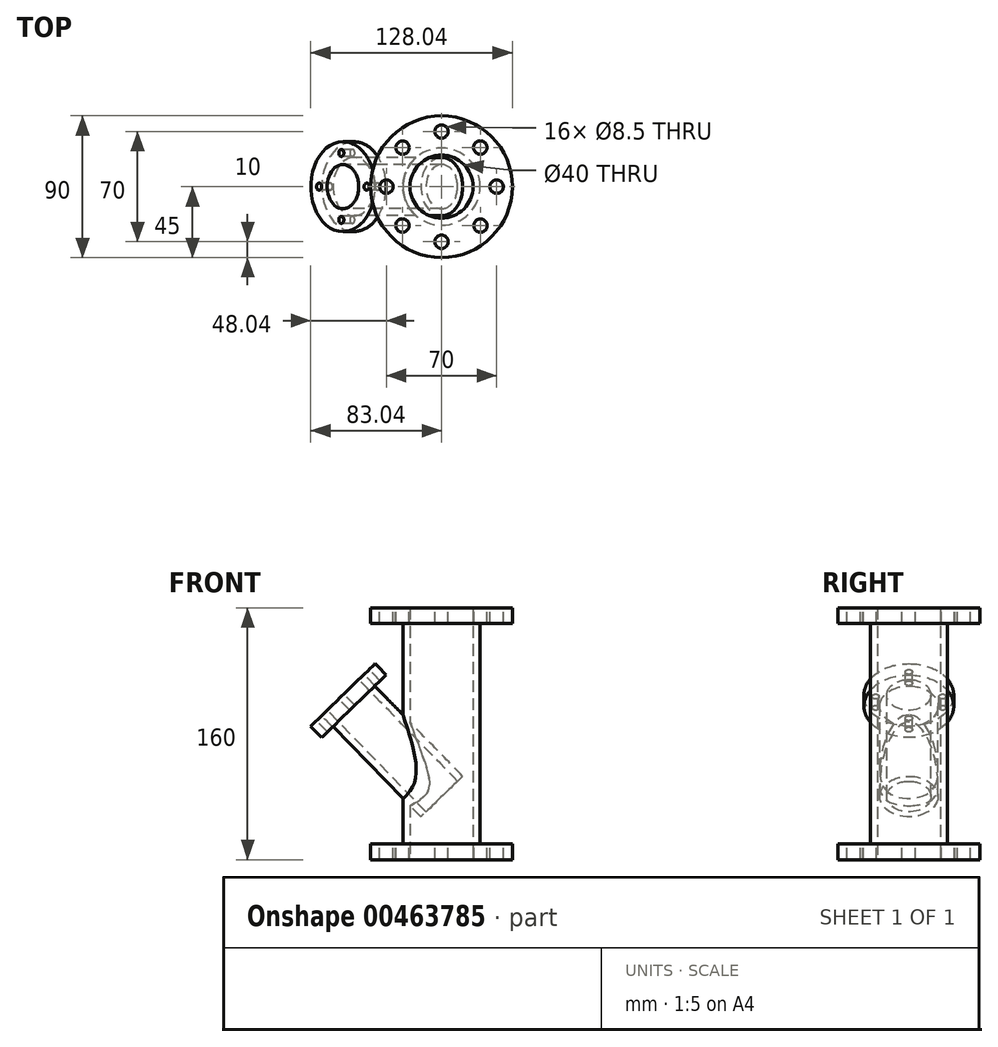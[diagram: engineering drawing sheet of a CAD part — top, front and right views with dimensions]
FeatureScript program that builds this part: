
annotation { "Feature Type Name" : "Feature", "Feature Type Description" : "" }
export const myFeature = defineFeature(function(context is Context, id is Id, definition is map)
    precondition{}
    {
        {
            var Q0;
            Q0=qCreatedBy(makeId("Top.planeOp"),FACE);
            var sketch = newSketch(context, id + "F0", { "sketchPlane" : qUnion([Q0])});
            skCircle(sketch, "E0", {"center": v(0, 0) * mm, "radius": 45 * mm});
            skSolve(sketch);
        }
        {
            var Q0;
            Q0=makeQuery(id+"F0.imprint","IMPRINT",FACE,{"disambiguationData":[TD([[makeQuery(id+"F0.imprint","IMPRINT",EDGE,{"derivedFrom":sQuery(id+"F0.wireOp",EDGE,"E0")}),1.0]])]});
            extrude(context, id + "F1", {"entities" : qUnion([Q0]), "depth" : 10 * mm});
        }
        {
            var Q0;
            Q0=makeQuery(id+"F1.opExtrude","CAP_FACE",FACE,{"disambiguationData":[OSD([sQuery(id+"F0.wireOp",EDGE,"E0")])],"isStart":false});
            var sketch = newSketch(context, id + "F2", { "sketchPlane" : qUnion([Q0])});
            skCircle(sketch, "E1", {"center": v(0, 0) * mm, "radius": 24.5 * mm});
            skCircle(sketch, "E2", {"center": v(0, 0) * mm, "radius": 20 * mm});
            skSolve(sketch);
        }
        {
            var Q0;
            Q0=makeQuery(id+"F2.imprint","IMPRINT",FACE,{"disambiguationData":[TD([[makeQuery(id+"F2.imprint","IMPRINT",EDGE,{"derivedFrom":sQuery(id+"F2.wireOp",EDGE,"E1")}),1.0]])]});
            extrude(context, id + "F3", {"entities" : qUnion([Q0]), "operationType" : NewBodyOperationType.ADD, "depth" : 140 * mm});
        }
        {
            var Q0;
            Q0=makeQuery(id+"F1.opExtrude","CAP_FACE",FACE,{"disambiguationData":[OSD([sQuery(id+"F0.wireOp",EDGE,"E0")])],"isStart":true});
            var sketch = newSketch(context, id + "F4", { "sketchPlane" : qUnion([Q0])});
            skCircle(sketch, "E3", {"center": v(0, 0) * mm, "radius": 20 * mm});
            skSolve(sketch);
        }
        {
            var Q0;
            Q0=makeQuery(id+"F4.imprint","IMPRINT",FACE,{"disambiguationData":[TD([[makeQuery(id+"F4.imprint","IMPRINT",EDGE,{"derivedFrom":sQuery(id+"F4.wireOp",EDGE,"E3")}),1.0]])]});
            extrude(context, id + "F5", {"entities" : qUnion([Q0]), "operationType" : NewBodyOperationType.REMOVE, "endBound" : BoundingType.THROUGH_ALL, "oppositeDirection" : true, "depth" : 25 * mm});
        }
        {
            var Q0;
            Q0=makeQuery(id+"F3.opExtrude","CAP_FACE",FACE,{"disambiguationData":[OSD([sQuery(id+"F2.wireOp",EDGE,"E1"),sQuery(id+"F2.wireOp",EDGE,"E2")])],"isStart":false});
            var sketch = newSketch(context, id + "F6", { "sketchPlane" : qUnion([Q0])});
            skCircle(sketch, "E4", {"center": v(0, 0) * mm, "radius": 45 * mm});
            skCircle(sketch, "E5", {"center": v(0, 0) * mm, "radius": 20 * mm});
            skSolve(sketch);
        }
        {
            var Q0;
            Q0 = qSketchRegion(id + "F6", true);
            extrude(context, id + "F7", {"entities" : qUnion([Q0]), "operationType" : NewBodyOperationType.ADD, "depth" : 10 * mm});
        }
        {
            var Q0;
            Q0=makeQuery(id+"F7.opExtrude","CAP_FACE",FACE,{"disambiguationData":[OSD([sQuery(id+"F6.wireOp",EDGE,"E4"),sQuery(id+"F6.wireOp",EDGE,"E5")])],"isStart":false});
            var sketch = newSketch(context, id + "F8", { "sketchPlane" : qUnion([Q0])});
            skCircle(sketch, "E6", {"center": v(0, 35) * mm, "radius": 4.25 * mm});
            skCircle(sketch, "E7", {"center": v(0, -35) * mm, "radius": 4.25 * mm});
            skCircle(sketch, "E8", {"center": v(35, 0) * mm, "radius": 4.25 * mm});
            skCircle(sketch, "E9", {"center": v(-35, 0) * mm, "radius": 4.25 * mm});
            skCircle(sketch, "E10", {"center": v(-24.73, 24.76) * mm, "radius": 4.25 * mm});
            skCircle(sketch, "E11", {"center": v(24.73, -24.76) * mm, "radius": 4.25 * mm});
            skCircle(sketch, "E12", {"center": v(24.64, 24.86) * mm, "radius": 4.25 * mm});
            skCircle(sketch, "E13", {"center": v(-24.83, -24.67) * mm, "radius": 4.25 * mm});
            skSolve(sketch);
        }
        {
            var Q0;
            Q0=makeQuery(id+"F8.imprint","IMPRINT",FACE,{"disambiguationData":[TD([[makeQuery(id+"F8.imprint","IMPRINT",EDGE,{"derivedFrom":sQuery(id+"F8.wireOp",EDGE,"E6")}),1.0]])]});
            var Q1;
            Q1=makeQuery(id+"F8.imprint","IMPRINT",FACE,{"disambiguationData":[TD([[makeQuery(id+"F8.imprint","IMPRINT",EDGE,{"derivedFrom":sQuery(id+"F8.wireOp",EDGE,"E7")}),1.0]])]});
            var Q2;
            Q2=makeQuery(id+"F8.imprint","IMPRINT",FACE,{"disambiguationData":[TD([[makeQuery(id+"F8.imprint","IMPRINT",EDGE,{"derivedFrom":sQuery(id+"F8.wireOp",EDGE,"E8")}),1.0]])]});
            var Q3;
            Q3=makeQuery(id+"F8.imprint","IMPRINT",FACE,{"disambiguationData":[TD([[makeQuery(id+"F8.imprint","IMPRINT",EDGE,{"derivedFrom":sQuery(id+"F8.wireOp",EDGE,"E9")}),1.0]])]});
            var Q4;
            Q4=makeQuery(id+"F8.imprint","IMPRINT",FACE,{"disambiguationData":[TD([[makeQuery(id+"F8.imprint","IMPRINT",EDGE,{"derivedFrom":sQuery(id+"F8.wireOp",EDGE,"E10")}),1.0]])]});
            var Q5;
            Q5=makeQuery(id+"F8.imprint","IMPRINT",FACE,{"disambiguationData":[TD([[makeQuery(id+"F8.imprint","IMPRINT",EDGE,{"derivedFrom":sQuery(id+"F8.wireOp",EDGE,"E11")}),1.0]])]});
            var Q6;
            Q6=makeQuery(id+"F8.imprint","IMPRINT",FACE,{"disambiguationData":[TD([[makeQuery(id+"F8.imprint","IMPRINT",EDGE,{"derivedFrom":sQuery(id+"F8.wireOp",EDGE,"E13")}),1.0]])]});
            var Q7;
            Q7=makeQuery(id+"F8.imprint","IMPRINT",FACE,{"disambiguationData":[TD([[makeQuery(id+"F8.imprint","IMPRINT",EDGE,{"derivedFrom":sQuery(id+"F8.wireOp",EDGE,"E12")}),1.0]])]});
            extrude(context, id + "F9", {"entities" : qUnion([Q0, Q1, Q2, Q3, Q4, Q5, Q6, Q7]), "operationType" : NewBodyOperationType.REMOVE, "endBound" : BoundingType.THROUGH_ALL, "oppositeDirection" : true, "depth" : 25 * mm});
        }
        {
            var Q0;
            Q0=qCreatedBy(makeId("Front.planeOp"),FACE);
            var sketch = newSketch(context, id + "F10", { "sketchPlane" : qUnion([Q0])});
            skLineSegment(sketch, "E14", {"start": v(-63.62, 103.65) * mm, "end": v(-43.2, 123.52) * mm});
            skLineSegment(sketch, "E15", {"start": v(-63.62, 103.65) * mm, "end": v(-84.05, 83.77) * mm});
            skSolve(sketch);
        }
        {
            var Q0;
            Q0=qCreatedBy(makeId("Right.planeOp"),FACE);
            var Q1;
            Q1=sQuery(id+"F10.wireOp",EDGE,"E15");
            cPlane(context, id + "F11", {"entities" : qUnion([Q0, Q1]), "cplaneType" : CPlaneType.LINE_ANGLE, "offset" : 25 * mm, "angle" : 0 * degree, "width" : 150 * mm, "height" : 150 * mm});
        }
        {
            var Q0;
            Q0=qCreatedBy(id+"F11.planeOp",FACE);
            var sketch = newSketch(context, id + "F12", { "sketchPlane" : qUnion([Q0])});
            skCircle(sketch, "E16", {"center": v(28.09, 0) * mm, "radius": 18.5 * mm});
            skSolve(sketch);
        }
        {
            var Q0;
            Q0 = qSketchRegion(id + "F12", true);
            extrude(context, id + "F13", {"entities" : qUnion([Q0]), "operationType" : NewBodyOperationType.ADD, "oppositeDirection" : true, "depth" : 90 * mm});
        }
        {
            var Q0;
            Q0=makeQuery(id+"F13.opExtrude","CAP_FACE",FACE,{"disambiguationData":[OSD([sQuery(id+"F12.wireOp",EDGE,"E16")])],"isStart":true});
            var sketch = newSketch(context, id + "F14", { "sketchPlane" : qUnion([Q0])});
            skCircle(sketch, "E17", {"center": v(28.09, 0) * mm, "radius": 28.5 * mm});
            skSolve(sketch);
        }
        {
            var Q0;
            Q0 = qSketchRegion(id + "F14", true);
            extrude(context, id + "F15", {"entities" : qUnion([Q0]), "operationType" : NewBodyOperationType.ADD, "oppositeDirection" : true, "depth" : 10 * mm});
        }
        {
            var Q0;
            Q0=makeQuery(id+"F15.boolean.opBoolean","MERGE",FACE,{"derivedFrom":[makeQuery(id+"F13.opExtrude","CAP_FACE",FACE,{"disambiguationData":[OSD([sQuery(id+"F12.wireOp",EDGE,"E16")])],"isStart":true}),makeQuery(id+"F15.opExtrude","CAP_FACE",FACE,{"disambiguationData":[OSD([sQuery(id+"F14.wireOp",EDGE,"E17")])],"isStart":true})]});
            var sketch = newSketch(context, id + "F16", { "sketchPlane" : qUnion([Q0])});
            skCircle(sketch, "E18", {"center": v(28.09, 0) * mm, "radius": 14 * mm});
            skSolve(sketch);
        }
        {
            var Q0;
            Q0=makeQuery(id+"F16.imprint","IMPRINT",FACE,{"disambiguationData":[TD([[makeQuery(id+"F16.imprint","IMPRINT",EDGE,{"derivedFrom":sQuery(id+"F16.wireOp",EDGE,"E18")}),1.0]])]});
            extrude(context, id + "F17", {"entities" : qUnion([Q0]), "operationType" : NewBodyOperationType.REMOVE, "oppositeDirection" : true, "depth" : 90 * mm});
        }
        {
            var Q0;
            Q0=makeQuery(id+"F15.boolean.opBoolean","MERGE",FACE,{"derivedFrom":[makeQuery(id+"F13.opExtrude","CAP_FACE",FACE,{"disambiguationData":[OSD([sQuery(id+"F12.wireOp",EDGE,"E16")])],"isStart":true}),makeQuery(id+"F15.opExtrude","CAP_FACE",FACE,{"disambiguationData":[OSD([sQuery(id+"F14.wireOp",EDGE,"E17")])],"isStart":true})]});
            var sketch = newSketch(context, id + "F18", { "sketchPlane" : qUnion([Q0])});
            skCircle(sketch, "E19", {"center": v(26.67, 21.45) * mm, "radius": 2.25 * mm});
            skCircle(sketch, "E20", {"center": v(6.9, 0) * mm, "radius": 2.25 * mm});
            skCircle(sketch, "E21", {"center": v(49.06, 0) * mm, "radius": 2.25 * mm});
            skCircle(sketch, "E22", {"center": v(26.67, -21.08) * mm, "radius": 2.25 * mm});
            skSolve(sketch);
        }
        {
            var Q0;
            Q0=makeQuery(id+"F18.imprint","IMPRINT",FACE,{"disambiguationData":[TD([[makeQuery(id+"F18.imprint","IMPRINT",EDGE,{"derivedFrom":sQuery(id+"F18.wireOp",EDGE,"E19")}),1.0]])]});
            var Q1;
            Q1=makeQuery(id+"F18.imprint","IMPRINT",FACE,{"disambiguationData":[TD([[makeQuery(id+"F18.imprint","IMPRINT",EDGE,{"derivedFrom":sQuery(id+"F18.wireOp",EDGE,"E20")}),1.0]])]});
            var Q2;
            Q2=makeQuery(id+"F18.imprint","IMPRINT",FACE,{"disambiguationData":[TD([[makeQuery(id+"F18.imprint","IMPRINT",EDGE,{"derivedFrom":sQuery(id+"F18.wireOp",EDGE,"E22")}),1.0]])]});
            var Q3;
            Q3=makeQuery(id+"F18.imprint","IMPRINT",FACE,{"disambiguationData":[TD([[makeQuery(id+"F18.imprint","IMPRINT",EDGE,{"derivedFrom":sQuery(id+"F18.wireOp",EDGE,"E21")}),1.0]])]});
            extrude(context, id + "F19", {"entities" : qUnion([Q0, Q1, Q2, Q3]), "operationType" : NewBodyOperationType.REMOVE, "oppositeDirection" : true, "depth" : 12 * mm});
        }
    });
